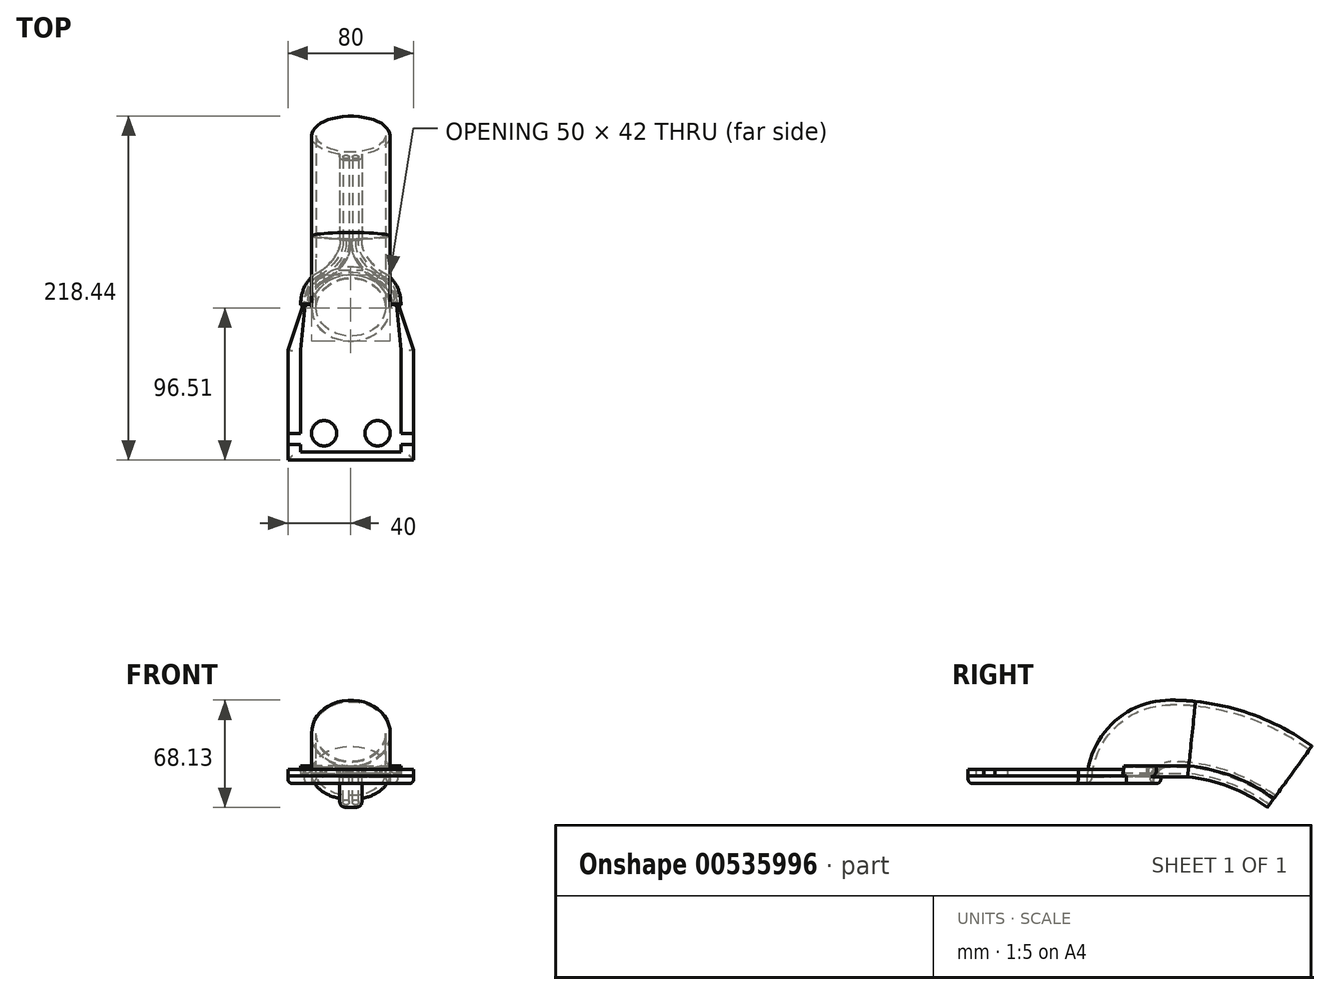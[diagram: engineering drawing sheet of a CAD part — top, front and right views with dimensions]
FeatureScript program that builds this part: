
annotation { "Feature Type Name" : "Feature", "Feature Type Description" : "" }
export const myFeature = defineFeature(function(context is Context, id is Id, definition is map)
    precondition{}
    {
        {
            var Q0;
            Q0=qCreatedBy(makeId("Top.planeOp"),FACE);
            var sketch = newSketch(context, id + "F0", { "sketchPlane" : qUnion([Q0])});
            skEllipse(sketch, "E0", {"center": v(0, 0) * mm, "majorRadius": 22 * mm, "minorRadius": 18 * mm, "majorAxis": v(1, 0)});
            skEllipse(sketch, "E1", {"center": v(0, 0) * mm, "majorRadius": 25 * mm, "minorRadius": 21 * mm, "majorAxis": v(-1, 0)});
            skLineSegment(sketch, "E2", {"start": v(-35.6, 32) * mm, "end": v(51.72, 32) * mm});
            skEllipse(sketch, "E3", {"center": v(0, 0) * mm, "majorRadius": 30 * mm, "minorRadius": 26 * mm, "majorAxis": v(-1, 0)});
            skLineSegment(sketch, "E4", {"start": v(-40, -26.5) * mm, "end": v(40, -26.5) * mm});
            skLineSegment(sketch, "E5", {"start": v(-40, -26.5) * mm, "end": v(-40, -96.5) * mm});
            skLineSegment(sketch, "E6", {"start": v(-40, -96.5) * mm, "end": v(40, -96.5) * mm});
            skLineSegment(sketch, "E7", {"start": v(40, -96.5) * mm, "end": v(40, -26.5) * mm});
            skLineSegment(sketch, "E8", {"start": v(40, -26.5) * mm, "end": v(29.63, 4.07) * mm});
            skLineSegment(sketch, "E9", {"start": v(-29.63, 4.07) * mm, "end": v(-40, -26.5) * mm});
            skLineSegment(sketch, "E10", {"start": v(-33.58, 0) * mm, "end": v(44.1, 0) * mm});
            skPoint(sketch, "E10.endSnap0", {"position": v(-30, 0) * mm});
            skPoint(sketch, "E11", {"position": v(6, 32) * mm});
            skPoint(sketch, "E12", {"position": v(30.7, 0.18) * mm});
            skFitSpline(sketch, "E13", {"points": [v(30.7, 0.18) * mm, v(19.37, 21.99) * mm], "startDerivative": vector(1.12, 29.83) * mm, "endDerivative": vector(-24.71, 12.22) * mm});
            skFitSpline(sketch, "E14", {"points": [v(19.37, 21.99) * mm, v(6, 41.41) * mm], "startDerivative": vector(-17.4, 12.98) * mm, "endDerivative": vector(-0.5, 24.65) * mm});
            skFitSpline(sketch, "E15.MirrorCS", {"points": [v(-19.37, 21.99) * mm, v(-6, 41.41) * mm], "startDerivative": vector(17.4, 12.98) * mm, "endDerivative": vector(0.5, 24.65) * mm});
            skFitSpline(sketch, "E16.MirrorCS", {"points": [v(-30.7, 0.18) * mm, v(-19.37, 21.99) * mm], "startDerivative": vector(-1.12, 29.83) * mm, "endDerivative": vector(24.71, 12.22) * mm});
            skSolve(sketch);
        }
        {
            var Q0;
            Q0=makeQuery(id+"F0.imprint","IMPRINT",FACE,{"disambiguationData":[TD([[makeQuery(id+"F0.imprint","IMPRINT",EDGE,{"derivedFrom":sQuery(id+"F0.wireOp",EDGE,"E0")}),-1.0]])]});
            var Q1;
            Q1=sQuery(id+"F0.wireOp",EDGE,"E2");
            revolve(context, id + "F1", {"entities" : qUnion([Q0]), "axis" : qUnion([Q1]), "revolveType" : RevolveType.ONE_DIRECTION, "oppositeDirection" : true, "angle" : 90 * degree});
        }
        {
            var Q0;
            Q0=makeQuery(id+"F0.imprint","IMPRINT",FACE,{"disambiguationData":[TD([[makeQuery(id+"F0.imprint","IMPRINT",EDGE,{"derivedFrom":sQuery(id+"F0.wireOp",EDGE,"E4")}),-1.0]])]});
            var Q1;
            Q1=makeQuery(id+"F0.imprint","IMPRINT",FACE,{"disambiguationData":[TD([[makeQuery(id+"F0.imprint","IMPRINT",EDGE,{"derivedFrom":sQuery(id+"F0.wireOp",EDGE,"E4")}),1.0]])]});
            var Q2;
            {var subQ0=sQuery(id+"F0.wireOp",EDGE,"E10");var subQ1=sQuery(id+"F0.wireOp",EDGE,"E1");var subQ2=makeQuery(id+"F0.imprint","INTERSECT",VERTEX,{"disambiguationData":[OD(0.0)],"derivedFrom":[subQ1,subQ0]});Q2=makeQuery(id+"F0.imprint","IMPRINT",FACE,{"disambiguationData":[TD([[makeQuery(id+"F0.imprint","IMPRINT",EDGE,{"disambiguationData":[TD([[subQ2,-1.0]])],"derivedFrom":subQ1}),-1.0]])]});}
            var Q3;
            {var subQ2=sQuery(id+"F0.wireOp",EDGE,"E10");var subQ5=sQuery(id+"F0.wireOp",EDGE,"E1");var subQ6=makeQuery(id+"F0.imprint","INTERSECT",VERTEX,{"disambiguationData":[OD(0.0)],"derivedFrom":[subQ5,subQ2]});Q3=makeQuery(id+"F0.imprint","IMPRINT",FACE,{"disambiguationData":[TD([[makeQuery(id+"F0.imprint","IMPRINT",EDGE,{"disambiguationData":[TD([[subQ6,1.0]])],"derivedFrom":subQ5}),-1.0]])]});}
            var Q4;
            {var subQ0=sQuery(id+"F0.wireOp",EDGE,"E9");var subQ1=sQuery(id+"F0.wireOp",EDGE,"E3");var subQ2=makeQuery(id+"F0.imprint","INTERSECT",VERTEX,{"derivedFrom":[subQ1,subQ0]});Q4=makeQuery(id+"F0.imprint","IMPRINT",FACE,{"disambiguationData":[TD([[makeQuery(id+"F0.imprint","IMPRINT",EDGE,{"disambiguationData":[TD([[subQ2,-1.0]])],"derivedFrom":subQ1}),-1.0]])]});}
            var Q5;
            {var subQ0=sQuery(id+"F0.wireOp",EDGE,"E8");var subQ1=sQuery(id+"F0.wireOp",EDGE,"E3");var subQ2=makeQuery(id+"F0.imprint","INTERSECT",VERTEX,{"derivedFrom":[subQ1,subQ0]});Q5=makeQuery(id+"F0.imprint","IMPRINT",FACE,{"disambiguationData":[TD([[makeQuery(id+"F0.imprint","IMPRINT",EDGE,{"disambiguationData":[TD([[subQ2,1.0]])],"derivedFrom":subQ1}),-1.0]])]});}
            var Q6;
            {var subQ0=sQuery(id+"F0.wireOp",EDGE,"E13");Q6=makeQuery(id+"F0.imprint","IMPRINT",FACE,{"disambiguationData":[TD([[makeQuery(id+"F0.imprint","IMPRINT",EDGE,{"derivedFrom":subQ0}),-1.0]])]});}
            extrude(context, id + "F2", {"entities" : qUnion([Q0, Q1, Q2, Q3, Q4, Q5, Q6]), "depth" : 5 * mm, "offsetDistance" : 25 * mm});
        }
        {
            var Q0;
            Q0=makeQuery(id+"F1.opRevolve","CAP_EDGE",EDGE,{"disambiguationData":[OSD([sQuery(id+"F0.wireOp",EDGE,"E0")])],"isStart":true});
            fillet(context, id + "F3", {"entities" : qUnion([Q0]), "radius" : 5 * mm, "tangentPropagation" : true, "allowEdgeOverflow" : false});
        }
        {
            var Q0;
            Q0=makeQuery(id+"F2.opExtrude","CAP_EDGE",EDGE,{"disambiguationData":[OSD([sQuery(id+"F0.wireOp",EDGE,"E3")])],"isStart":true});
            var Q1;
            Q1=makeQuery(id+"F2.opExtrude","CAP_EDGE",EDGE,{"disambiguationData":[OSD([sQuery(id+"F0.wireOp",EDGE,"E9")])],"isStart":true});
            var Q2;
            Q2=makeQuery(id+"F2.opExtrude","CAP_EDGE",EDGE,{"disambiguationData":[OSD([sQuery(id+"F0.wireOp",EDGE,"E8")])],"isStart":true});
            var Q3;
            Q3=makeQuery(id+"F2.opExtrude","CAP_EDGE",EDGE,{"disambiguationData":[OSD([sQuery(id+"F0.wireOp",EDGE,"E5")])],"isStart":true});
            var Q4;
            Q4=makeQuery(id+"F2.opExtrude","CAP_EDGE",EDGE,{"disambiguationData":[OSD([sQuery(id+"F0.wireOp",EDGE,"E6")])],"isStart":true});
            var Q5;
            Q5=makeQuery(id+"F2.opExtrude","CAP_EDGE",EDGE,{"disambiguationData":[OSD([sQuery(id+"F0.wireOp",EDGE,"E7")])],"isStart":true});
            fillet(context, id + "F4", {"entities" : qUnion([Q0, Q1, Q2, Q3, Q4, Q5]), "radius" : 3 * mm, "tangentPropagation" : true, "allowEdgeOverflow" : false});
        }
        {
            var Q0;
            Q0=makeQuery(id+"F1.opRevolve","CAP_FACE",FACE,{"disambiguationData":[OSD([sQuery(id+"F0.wireOp",EDGE,"E0"),sQuery(id+"F0.wireOp",EDGE,"E1")])],"isStart":false});
            var sketch = newSketch(context, id + "F5", { "sketchPlane" : qUnion([Q0])});
            skLineSegment(sketch, "E17", {"start": v(-62.24, -100) * mm, "end": v(76.42, -100) * mm});
            skPoint(sketch, "E18.endSnap0", {"position": v(0, 11) * mm});
            skSolve(sketch);
        }
        {
            var Q0;
            Q0=makeQuery(id+"F5.imprint","IMPRINT",FACE,{"disambiguationData":[TD([[makeQuery(id+"F5.imprint","IMPRINT",EDGE,{"derivedFrom":makeQuery(id+"F1.opRevolve","CAP_EDGE",EDGE,{"disambiguationData":[OSD([sQuery(id+"F0.wireOp",EDGE,"E0")])],"isStart":false})}),-1.0]])]});
            var Q1;
            {var subQ0=sQuery(id+"F5.wireOp",EDGE,"U0pvSwCb-7xu7-HrN8-dMLj-IvFatY6Amtoi");var subQ1=makeQuery(id+"F1.opRevolve","CAP_EDGE",EDGE,{"disambiguationData":[OSD([sQuery(id+"F0.wireOp",EDGE,"E1")])],"isStart":false});var subQ2=makeQuery(id+"F5.imprint","INTERSECT",VERTEX,{"derivedFrom":[subQ1,subQ0,sQuery(id+"F5.wireOp",EDGE,"HCc1UObz-Wg3N-9KnM-nclE-zhxUFfY4LmUf")]});Q1=makeQuery(id+"F5.imprint","IMPRINT",FACE,{"disambiguationData":[TD([[makeQuery(id+"F5.imprint","IMPRINT",EDGE,{"disambiguationData":[TD([[subQ2,-1.0]])],"derivedFrom":subQ0}),-1.0]])]});}
            var Q2;
            Q2=makeQuery(id+"F5.imprint","IMPRINT",FACE,{"disambiguationData":[TD([[makeQuery(id+"F5.imprint","IMPRINT",EDGE,{"derivedFrom":sQuery(id+"F5.wireOp",EDGE,"026SiKdb-LZOD-O7N3-xJ5z-ZswVnRoNnFCt")}),-1.0]])]});
            var Q3;
            Q3=sQuery(id+"F5.wireOp",EDGE,"E17");
            revolve(context, id + "F6", {"operationType" : NewBodyOperationType.ADD, "entities" : qUnion([Q0, Q1, Q2]), "axis" : qUnion([Q3]), "revolveType" : RevolveType.ONE_DIRECTION, "angle" : 6 * degree});
        }
        {
            var Q0;
            Q0=makeQuery(id+"F6.opRevolve","CAP_FACE",FACE,{"disambiguationData":[OSD([sQuery(id+"F0.wireOp",EDGE,"E0"),sQuery(id+"F0.wireOp",EDGE,"E1")])],"isStart":false});
            var sketch = newSketch(context, id + "F7", { "sketchPlane" : qUnion([Q0])});
            skCircle(sketch, "E19", {"center": v(-3, 12.8) * mm, "radius": 2 * mm});
            skArc(sketch, "E20", {"start": v(-3, 8.8) * mm, "mid": v(-5.83, 9.97) * mm, "end": v(-7, 12.8) * mm});
            skCircle(sketch, "E21", {"center": v(3, 12.8) * mm, "radius": 2 * mm});
            skArc(sketch, "E22", {"start": v(3, 8.8) * mm, "mid": v(5.83, 9.97) * mm, "end": v(7, 12.8) * mm});
            skLineSegment(sketch, "E23", {"start": v(-3, 8.8) * mm, "end": v(3, 8.8) * mm});
            skLineSegment(sketch, "E24", {"start": v(-7, 12.8) * mm, "end": v(-7, 15.73) * mm});
            skLineSegment(sketch, "E25", {"start": v(7, 12.8) * mm, "end": v(7, 15.73) * mm});
            skLineSegment(sketch, "E26", {"start": v(0, 14.9) * mm, "end": v(0, 8.8) * mm});
            skSolve(sketch);
        }
        {
            var Q0;
            Q0=makeQuery(id+"F7.imprint","IMPRINT",FACE,{"disambiguationData":[TD([[makeQuery(id+"F7.imprint","IMPRINT",EDGE,{"derivedFrom":makeQuery(id+"F6.opRevolve","CAP_EDGE",EDGE,{"disambiguationData":[OSD([sQuery(id+"F0.wireOp",EDGE,"E0")])],"isStart":false})}),-1.0]])]});
            var Q1;
            Q1=makeQuery(id+"F7.imprint","IMPRINT",FACE,{"disambiguationData":[TD([[makeQuery(id+"F7.imprint","IMPRINT",EDGE,{"derivedFrom":sQuery(id+"F7.wireOp",EDGE,"E19")}),-1.0]])]});
            var Q2;
            Q2=makeQuery(id+"F7.imprint","IMPRINT",FACE,{"disambiguationData":[TD([[makeQuery(id+"F7.imprint","IMPRINT",EDGE,{"derivedFrom":sQuery(id+"F7.wireOp",EDGE,"E21")}),-1.0]])]});
            var Q3;
            Q3=sQuery(id+"F5.wireOp",EDGE,"E17");
            revolve(context, id + "F8", {"entities" : qUnion([Q0, Q1, Q2]), "axis" : qUnion([Q3]), "revolveType" : RevolveType.ONE_DIRECTION, "angle" : 30 * degree});
        }
        {
            var Q0;
            Q0=makeQuery(id+"F7.imprint","IMPRINT",FACE,{"disambiguationData":[TD([[makeQuery(id+"F7.imprint","IMPRINT",EDGE,{"derivedFrom":sQuery(id+"F7.wireOp",EDGE,"E19")}),-1.0]])]});
            var Q1;
            Q1=sQuery(id+"F0.wireOp",EDGE,"E14");
            var Q2;
            Q2=sQuery(id+"F0.wireOp",EDGE,"E13");
            sweep(context, id + "F9", {"profiles" : qUnion([Q0]), "path" : qUnion([Q1, Q2])});
        }
        {
            var Q0;
            Q0=makeQuery(id+"F7.imprint","IMPRINT",FACE,{"disambiguationData":[TD([[makeQuery(id+"F7.imprint","IMPRINT",EDGE,{"derivedFrom":sQuery(id+"F7.wireOp",EDGE,"E21")}),-1.0]])]});
            var Q1;
            Q1=sQuery(id+"F0.wireOp",EDGE,"E15.MirrorCS");
            var Q2;
            Q2=sQuery(id+"F0.wireOp",EDGE,"E16.MirrorCS");
            sweep(context, id + "F10", {"profiles" : qUnion([Q0]), "path" : qUnion([Q1, Q2])});
        }
        {
            var Q0;
            Q0=makeQuery(id+"F2.opExtrude","CAP_FACE",FACE,{"disambiguationData":[OSD([sQuery(id+"F0.wireOp",EDGE,"E1"),sQuery(id+"F0.wireOp",EDGE,"E3"),sQuery(id+"F0.wireOp",EDGE,"E5"),sQuery(id+"F0.wireOp",EDGE,"E6"),sQuery(id+"F0.wireOp",EDGE,"E7"),sQuery(id+"F0.wireOp",EDGE,"E8"),sQuery(id+"F0.wireOp",EDGE,"E9")])],"isStart":false});
            var sketch = newSketch(context, id + "F11", { "sketchPlane" : qUnion([Q0])});
            skCircle(sketch, "E27", {"center": v(-17, -79.5) * mm, "radius": 8 * mm});
            skLineSegment(sketch, "E28", {"start": v(-40, -91.5) * mm, "end": v(40, -91.5) * mm});
            skLineSegment(sketch, "E29", {"start": v(-32, -91.5) * mm, "end": v(-32, -86.5) * mm});
            skLineSegment(sketch, "E30", {"start": v(-32, -86.5) * mm, "end": v(-40, -86.5) * mm});
            skLineSegment(sketch, "E31", {"start": v(-40, -79.5) * mm, "end": v(-32, -79.5) * mm});
            skLineSegment(sketch, "E32", {"start": v(-32, -79.5) * mm, "end": v(-32, -26.5) * mm});
            skLineSegment(sketch, "E33", {"start": v(-32, -26.5) * mm, "end": v(-40, -26.5) * mm});
            skLineSegment(sketch, "E34", {"start": v(-32, -26.5) * mm, "end": v(-29.05, 2.04) * mm});
            skLineSegment(sketch, "E35", {"start": v(-29.05, 2.04) * mm, "end": v(-30.32, 2.04) * mm});
            skLineSegment(sketch, "E36", {"start": v(0, 0) * mm, "end": v(0, -129.1) * mm});
            skPoint(sketch, "E36.endSnap0", {"position": v(0, -21) * mm});
            skCircle(sketch, "E37.MirrorC", {"center": v(17, -79.5) * mm, "radius": 8 * mm});
            skLineSegment(sketch, "E38.MirrorCS", {"start": v(32, -91.5) * mm, "end": v(32, -86.5) * mm});
            skLineSegment(sketch, "E39.MirrorCS", {"start": v(32, -86.5) * mm, "end": v(40, -86.5) * mm});
            skLineSegment(sketch, "E40.MirrorCS", {"start": v(32, -79.5) * mm, "end": v(32, -26.5) * mm});
            skLineSegment(sketch, "E41.MirrorCS", {"start": v(40, -79.5) * mm, "end": v(32, -79.5) * mm});
            skLineSegment(sketch, "E42.MirrorCS", {"start": v(32, -26.5) * mm, "end": v(40, -26.5) * mm});
            skLineSegment(sketch, "E43.MirrorCS", {"start": v(32, -26.5) * mm, "end": v(29.05, 2.04) * mm});
            skLineSegment(sketch, "E44.MirrorCS", {"start": v(29.05, 2.04) * mm, "end": v(30.32, 2.04) * mm});
            skSolve(sketch);
        }
        {
            var Q0;
            Q0 = qSketchRegion(id + "F11", true);
            var Q1;
            {var subQ0=sQuery(id+"F11.wireOp",EDGE,"E33");Q1=makeQuery(id+"F11.imprint","IMPRINT",FACE,{"disambiguationData":[TD([[makeQuery(id+"F11.imprint","IMPRINT",EDGE,{"derivedFrom":subQ0}),-1.0]])]});}
            var Q2;
            {var subQ0=sQuery(id+"F11.wireOp",EDGE,"E31");Q2=makeQuery(id+"F11.imprint","IMPRINT",FACE,{"disambiguationData":[TD([[makeQuery(id+"F11.imprint","IMPRINT",EDGE,{"derivedFrom":subQ0}),1.0]])]});}
            var Q3;
            {var subQ3=sQuery(id+"F11.wireOp",EDGE,"E29");Q3=makeQuery(id+"F11.imprint","IMPRINT",FACE,{"disambiguationData":[TD([[makeQuery(id+"F11.imprint","IMPRINT",EDGE,{"derivedFrom":subQ3}),1.0]])]});}
            var Q4;
            {var subQ0=makeQuery(id+"F2.opExtrude","CAP_EDGE",EDGE,{"disambiguationData":[OSD([sQuery(id+"F0.wireOp",EDGE,"E6")])],"isStart":false});Q4=makeQuery(id+"F11.imprint","IMPRINT",FACE,{"disambiguationData":[TD([[makeQuery(id+"F11.imprint","IMPRINT",EDGE,{"derivedFrom":subQ0}),1.0]])]});}
            var Q5;
            {var subQ3=sQuery(id+"F11.wireOp",EDGE,"E38.MirrorCS");Q5=makeQuery(id+"F11.imprint","IMPRINT",FACE,{"disambiguationData":[TD([[makeQuery(id+"F11.imprint","IMPRINT",EDGE,{"derivedFrom":subQ3}),-1.0]])]});}
            var Q6;
            Q6=makeQuery(id+"F11.imprint","IMPRINT",FACE,{"disambiguationData":[TD([[makeQuery(id+"F11.imprint","IMPRINT",EDGE,{"derivedFrom":sQuery(id+"F11.wireOp",EDGE,"E40.MirrorCS")}),-1.0]])]});
            var Q7;
            {var subQ0=sQuery(id+"F11.wireOp",EDGE,"E42.MirrorCS");Q7=makeQuery(id+"F11.imprint","IMPRINT",FACE,{"disambiguationData":[TD([[makeQuery(id+"F11.imprint","IMPRINT",EDGE,{"derivedFrom":subQ0}),1.0]])]});}
            extrude(context, id + "F12", {"entities" : qUnion([Q0, Q1, Q2, Q3, Q4, Q5, Q6, Q7]), "depth" : 4 * mm, "offsetDistance" : 25 * mm});
        }
        {
            var Q0;
            Q0=makeQuery(id+"F10.opSweep","SWEPT_FACE",FACE,{"disambiguationData":[OSD([sQuery(id+"F0.wireOp",EDGE,"E15.MirrorCS"),sQuery(id+"F7.wireOp",EDGE,"E23")])]});
            var sketch = newSketch(context, id + "F13", { "sketchPlane" : qUnion([Q0])});
            skLineSegment(sketch, "E45", {"start": v(-7.78, -24.28) * mm, "end": v(0, -24.28) * mm});
            skLineSegment(sketch, "E46", {"start": v(0, -24.28) * mm, "end": v(0, -42.97) * mm});
            skLineSegment(sketch, "E47.MirrorCS", {"start": v(7.78, -24.28) * mm, "end": v(0, -24.28) * mm});
            skFitSpline(sketch, "E48", {"points": [v(-7.78, -24.28) * mm, v(0, -42.97) * mm], "startDerivative": vector(16.1, -22.73) * mm, "endDerivative": vector(1.94, -28.68) * mm});
            skFitSpline(sketch, "E49.MirrorCS", {"points": [v(7.78, -24.28) * mm, v(0, -42.97) * mm], "startDerivative": vector(-16.1, -22.73) * mm, "endDerivative": vector(-1.94, -28.68) * mm});
            skSolve(sketch);
        }
        {
            var Q0;
            {var subQ0=sQuery(id+"F13.wireOp",EDGE,"E45");Q0=makeQuery(id+"F13.imprint","IMPRINT",FACE,{"disambiguationData":[TD([[makeQuery(id+"F13.imprint","IMPRINT",EDGE,{"derivedFrom":subQ0}),-1.0]])]});}
            var Q1;
            {var subQ0=sQuery(id+"F13.wireOp",EDGE,"E47.MirrorCS");Q1=makeQuery(id+"F13.imprint","IMPRINT",FACE,{"disambiguationData":[TD([[makeQuery(id+"F13.imprint","IMPRINT",EDGE,{"derivedFrom":subQ0}),1.0]])]});}
            extrude(context, id + "F14", {"entities" : qUnion([Q0, Q1]), "endBound" : BoundingType.UP_TO_NEXT, "oppositeDirection" : true, "depth" : 25 * mm, "offsetDistance" : 25 * mm});
        }
    });
